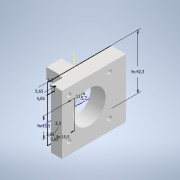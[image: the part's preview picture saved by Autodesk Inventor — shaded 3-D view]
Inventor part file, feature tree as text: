
AUTODESK INVENTOR PART (.ipt)
format: ipt  version: 2022.2 (Build 262287000, 287)  size: 2,201,600 bytes
history: native  units: mm
features: sketch x13, extrude x7, other x4, projected_geometry x3, hole x2, thread x2, revolve x2, helix x2, fillet x1, plane x1, reference x1
ambient origin geometry x8: Origin, YZ Plane, XZ Plane, XY Plane, X Axis, Y Axis, Z Axis, Center Point
bodies: Solid1 (feature_tree), Solid2 (feature_tree), Solid3 (feature_tree)
feature tree (38):
  other  "Motor.ipt"
  extrude  "Extrusion1"  Depth=10.0mm
  extrude  "Extrusion2"  Depth=3.3mm
  extrude  "Extrusion4"  Depth=15.500005mm
  extrude  "Extrusion5"  Depth=5.65mm
  fillet  "Fillet1"  Radius=11.5mm
  hole  "Hole1"  [1 undecoded]
  thread  "Thread1"  [1 undecoded]
  thread  "Thread2"  [1 undecoded]
  sketch  "Sketch8"  dims[d17=5.65mm d18=5.65mm]
  plane  "Work Plane1"
  extrude  "Extrusion6"  Depth=5.65mm
  extrude  "Extrusion7"  Depth=5.2mm
  revolve  "Revolution1"  [1 undecoded]
  helix  "Coil1"  [1 undecoded]
  revolve  "Revolution2"  [1 undecoded]
  helix  "Coil2"  [1 undecoded]
  hole  "Hole2"  [1 undecoded]
  extrude  "Extrusion8"  TaperAngle=0.0deg  [1 undecoded]
  sketch  "Sketch2"  dims[d0=10.0mm d1=11.0mm]
  sketch  "Sketch3"  dims[d2=5.7mm d3=3.3mm]
  projected_geometry  "Projected Loop1"
  sketch  "Sketch5"  dims[d4=15.500005mm d5=15.500005mm]
  sketch  "Sketch6"  dims[d6=5.65mm d7=5.65mm d8=11.5mm d9=0.0mm]
  projected_geometry  "Projected Loop2"
  sketch  "Sketch7"  dims[d10=25.0mm d11=2.4mm d12=0.0mm d15=42.3mm d16=3.3mm]
  projected_geometry  "Projected Loop4"
  sketch  "Sketch9"  dims[d22=10.5mm d23=0.0mm d24=5.2mm]
  reference  "Reference1"
  sketch  "Sketch10"  dims[d25=4.0mm d26=0.0mm d27=1.0mm]
  sketch  "Sketch11"  dims[d28=3.18mm d29=6.0mm d30=4.0mm d31=2.0mm d32=90.0deg d33=8.0mm d34=20.594885mm d35=8.0mm d36=0.0mm]
  sketch  "Sketch12"  dims[d37=8.0mm d38=0.0mm d39=5.0mm d40=0.0mm d41=3.0mm d42=0.0mm]
  sketch  "Sketch13"  dims[d43=9.599311mm d44=0.080042mm d45=0.080042mm d48=0.5mm]
  sketch  "Sketch14"  dims[d50=9.599311mm d52=0.0mm]
  sketch  "Sketch15"  dims[d53=0.5005mm d54=9.0mm d55=10.0mm d56=0.0mm d57=0.0mm d58=0.0mm d59=0.0mm d60=0.0mm d61=9.599311mm d62=0.080042mm d63=0.080042mm d66=0.5mm d68=9.599311mm d70=0.0mm d71=0.5005mm d72=9.0mm d73=10.0mm d74=0.0mm d75=0.0mm d76=0.0mm d77=0.0mm d78=0.0mm d79=31.000011mm d80=31.000011mm d81=3.18mm d82=6.0mm d83=6.0mm d84=4.0mm d85=90.0deg d86=8.0mm d87=20.594885mm d88=8.0mm d89=3.0mm d90=0.0mm d91=17.0mm d92=6.0mm]
  other  "<userpath>\Documents\Inventor\Wire Bender\Assembly.iam"
  other  "Assembly.iam"
  other  "Bending Base:1"
note: 9 required parameter values undecoded (feature->parameter linkage not recoverable at this tier; creation-order binding heuristic only, values carry confidence <= 0.55)